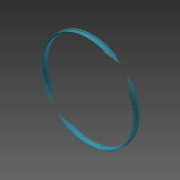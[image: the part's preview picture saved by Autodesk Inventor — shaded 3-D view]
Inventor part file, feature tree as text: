
AUTODESK INVENTOR PART (.ipt)
format: ipt  version: 2015 (Build 190159000, 159)  size: 1,152,000 bytes
history: native  units: mm
features: other x7, hole x4, sketch x4, pattern_circular x3
ambient origin geometry x8: Origin, YZ Plane, XZ Plane, XY Plane, X Axis, Y Axis, Z Axis, Center Point
bodies: Body1 (feature_tree)
feature tree (18):
  other  "Bryła1"
  other  "Obręcz"
  other  "Płaszczyzna do otworu na nypel 1"
  hole  "Otwór na nypel 1"  [1 undecoded]
  pattern_circular  "Szyk otworów na nypel 1"  [2 undecoded]
  other  "Płaszczyzna do otworu na nypel 2"
  other  "Płaszczyzna do otworu na nypel 2.2"
  hole  "Otwór na nypel 2"  [1 undecoded]
  pattern_circular  "Szyk otworów na nypel 2"  [2 undecoded]
  other  "Płaszczyzna do otworu na wentyl"
  hole  "Otwór na wentyl"  [1 undecoded]
  other  "Płaszczyzna konstrukcyjna5"
  hole  "Otwór7"  [1 undecoded]
  pattern_circular  "Szyk kołowy5"  [2 undecoded]
  sketch  "Szkic1"
  sketch  "Szkic4"
  sketch  "Szkic6"
  sketch  "Szkic7"
note: 10 required parameter values undecoded (feature->parameter linkage not recoverable at this tier; creation-order binding heuristic only, values carry confidence <= 0.55)
